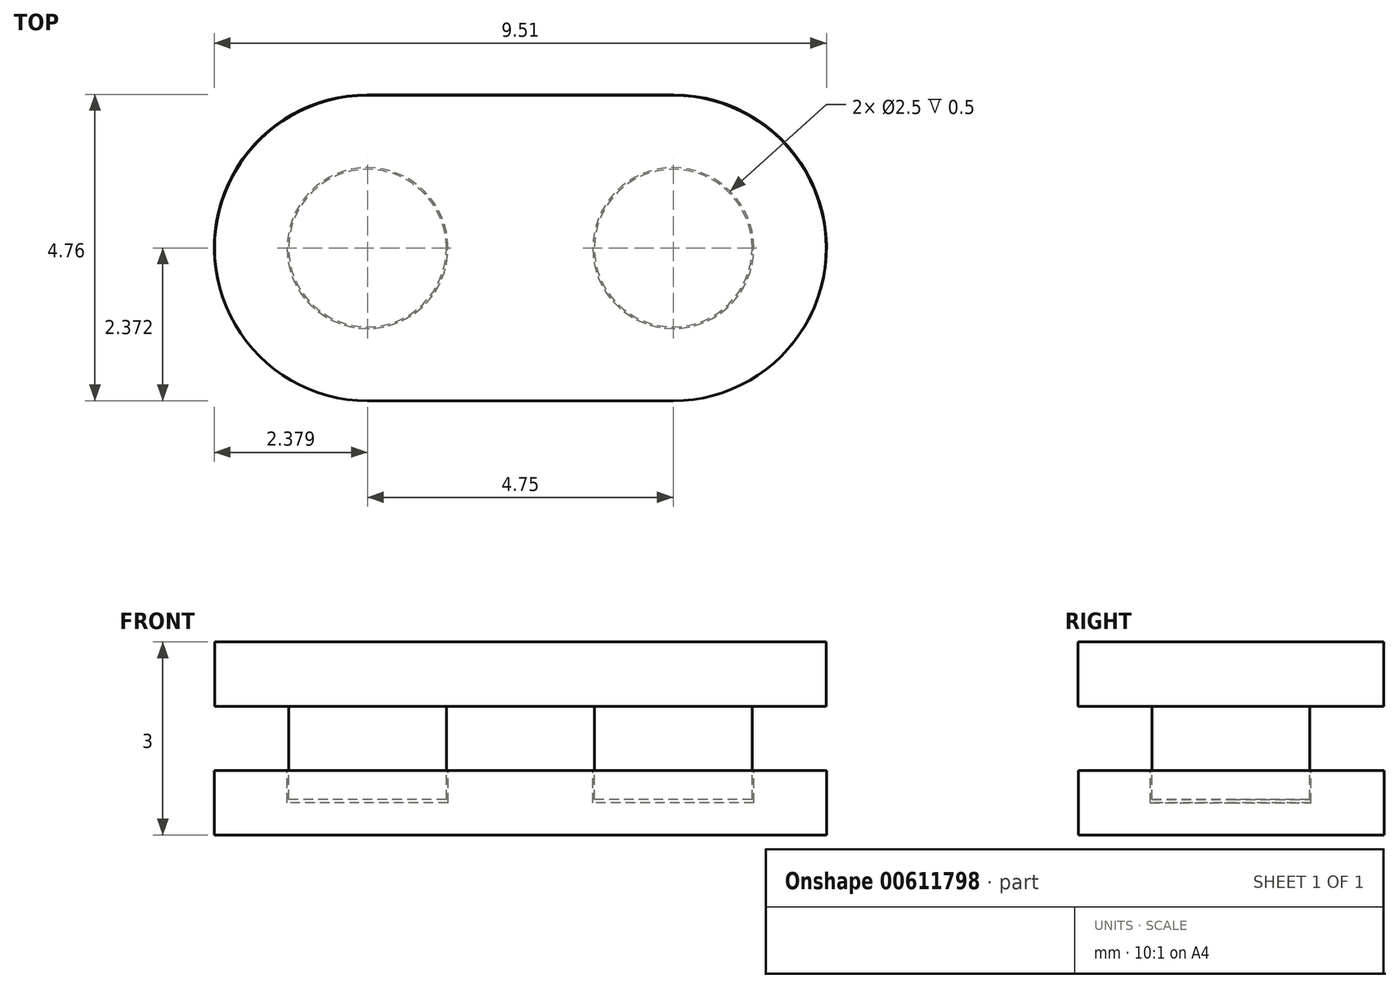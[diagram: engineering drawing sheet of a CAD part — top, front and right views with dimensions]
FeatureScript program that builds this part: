
annotation { "Feature Type Name" : "Feature", "Feature Type Description" : "" }
export const myFeature = defineFeature(function(context is Context, id is Id, definition is map)
    precondition{}
    {
        {
            var Q0;
            Q0=qCreatedBy(makeId("Top.planeOp"),FACE);
            var sketch = newSketch(context, id + "F0", { "sketchPlane" : qUnion([Q0])});
            skArc(sketch, "E0", {"start": v(2.64, -2.38) * mm, "mid": v(5.01, 0) * mm, "end": v(2.64, 2.37) * mm});
            skLineSegment(sketch, "E1", {"start": v(2.64, 2.37) * mm, "end": v(0.26, 2.37) * mm});
            skLineSegment(sketch, "E2", {"start": v(2.64, -2.38) * mm, "end": v(0.26, -2.38) * mm});
            skLineSegment(sketch, "E3.MirrorCS", {"start": v(-2.11, 2.37) * mm, "end": v(0.26, 2.37) * mm});
            skLineSegment(sketch, "E4.MirrorCS", {"start": v(-2.11, -2.38) * mm, "end": v(0.26, -2.38) * mm});
            skArc(sketch, "E5.MirrorC", {"start": v(-2.11, -2.38) * mm, "mid": v(-4.49, 0) * mm, "end": v(-2.11, 2.37) * mm});
            skCircle(sketch, "E6", {"center": v(-2.11, 0) * mm, "radius": 1.23 * mm});
            skCircle(sketch, "E7", {"center": v(2.64, 0) * mm, "radius": 1.23 * mm});
            skCircle(sketch, "E8", {"center": v(-2.11, 0) * mm, "radius": 1.25 * mm});
            skCircle(sketch, "E9", {"center": v(2.64, 0) * mm, "radius": 1.25 * mm});
            skSolve(sketch);
        }
        {
            var Q0;
            Q0 = qSketchRegion(id + "F0", true);
            var Q1;
            Q1=makeQuery(id+"F0.imprint","IMPRINT",FACE,{"disambiguationData":[TD([[makeQuery(id+"F0.imprint","IMPRINT",EDGE,{"derivedFrom":sQuery(id+"F0.wireOp",EDGE,"E6")}),1.0]])]});
            var Q2;
            Q2=makeQuery(id+"F0.imprint","IMPRINT",FACE,{"disambiguationData":[TD([[makeQuery(id+"F0.imprint","IMPRINT",EDGE,{"derivedFrom":sQuery(id+"F0.wireOp",EDGE,"E7")}),1.0]])]});
            var Q3;
            Q3=makeQuery(id+"F0.imprint","IMPRINT",FACE,{"disambiguationData":[TD([[makeQuery(id+"F0.imprint","IMPRINT",EDGE,{"derivedFrom":sQuery(id+"F0.wireOp",EDGE,"E7")}),-1.0]])]});
            var Q4;
            Q4=makeQuery(id+"F0.imprint","IMPRINT",FACE,{"disambiguationData":[TD([[makeQuery(id+"F0.imprint","IMPRINT",EDGE,{"derivedFrom":sQuery(id+"F0.wireOp",EDGE,"E6")}),-1.0]])]});
            extrude(context, id + "F1", {"entities" : qUnion([Q0, Q1, Q2, Q3, Q4]), "depth" : 1 * mm, "offsetDistance" : 25 * mm});
        }
        {
            var Q0;
            Q0=makeQuery(id+"F0.imprint","IMPRINT",FACE,{"disambiguationData":[TD([[makeQuery(id+"F0.imprint","IMPRINT",EDGE,{"derivedFrom":sQuery(id+"F0.wireOp",EDGE,"E7")}),1.0]])]});
            var Q1;
            Q1=makeQuery(id+"F0.imprint","IMPRINT",FACE,{"disambiguationData":[TD([[makeQuery(id+"F0.imprint","IMPRINT",EDGE,{"derivedFrom":sQuery(id+"F0.wireOp",EDGE,"E6")}),1.0]])]});
            extrude(context, id + "F2", {"entities" : qUnion([Q0, Q1]), "operationType" : NewBodyOperationType.ADD, "oppositeDirection" : true, "depth" : 1.5 * mm, "offsetDistance" : 25 * mm});
        }
        {
            var Q0;
            Q0=makeQuery(id+"F2.opExtrude","CAP_FACE",FACE,{"disambiguationData":[OSD([sQuery(id+"F0.wireOp",EDGE,"E6")])],"isStart":false});
            var sketch = newSketch(context, id + "F3", { "sketchPlane" : qUnion([Q0])});
            skArc(sketch, "E10", {"start": v(-2.12, 2.37) * mm, "mid": v(-4.5, 0) * mm, "end": v(-2.12, -2.38) * mm});
            skArc(sketch, "E11", {"start": v(2.65, -2.38) * mm, "mid": v(5.02, 0) * mm, "end": v(2.65, 2.38) * mm});
            skLineSegment(sketch, "E12", {"start": v(-2.12, 2.37) * mm, "end": v(2.65, 2.38) * mm});
            skLineSegment(sketch, "E13", {"start": v(-2.12, -2.38) * mm, "end": v(2.65, -2.37) * mm});
            skSolve(sketch);
        }
        {
            var Q0;
            Q0=makeQuery(id+"F3.imprint","IMPRINT",FACE,{"disambiguationData":[TD([[makeQuery(id+"F3.imprint","IMPRINT",EDGE,{"derivedFrom":sQuery(id+"F3.wireOp",EDGE,"E10")}),1.0]])]});
            var Q1;
            Q1=makeQuery(id+"F3.imprint","IMPRINT",FACE,{"disambiguationData":[TD([[makeQuery(id+"F3.imprint","IMPRINT",EDGE,{"derivedFrom":makeQuery(id+"F2.opExtrude","CAP_EDGE",EDGE,{"disambiguationData":[OSD([sQuery(id+"F0.wireOp",EDGE,"E6")])],"isStart":false})}),-1.0]])]});
            extrude(context, id + "F4", {"entities" : qUnion([Q0, Q1]), "depth" : .5 * mm, "offsetDistance" : 25 * mm, "hasSecondDirection" : true, "secondDirectionOppositeDirection" : true, "secondDirectionDepth" : .5 * mm});
        }
        {
            var Q0;
            Q0=makeQuery(id+"F0.imprint","IMPRINT",FACE,{"disambiguationData":[TD([[makeQuery(id+"F0.imprint","IMPRINT",EDGE,{"derivedFrom":sQuery(id+"F0.wireOp",EDGE,"E7")}),1.0]])]});
            var Q1;
            Q1=makeQuery(id+"F0.imprint","IMPRINT",FACE,{"disambiguationData":[TD([[makeQuery(id+"F0.imprint","IMPRINT",EDGE,{"derivedFrom":sQuery(id+"F0.wireOp",EDGE,"E6")}),1.0]])]});
            var Q2;
            Q2=makeQuery(id+"F0.imprint","IMPRINT",FACE,{"disambiguationData":[TD([[makeQuery(id+"F0.imprint","IMPRINT",EDGE,{"derivedFrom":sQuery(id+"F0.wireOp",EDGE,"E7")}),-1.0]])]});
            var Q3;
            Q3=makeQuery(id+"F0.imprint","IMPRINT",FACE,{"disambiguationData":[TD([[makeQuery(id+"F0.imprint","IMPRINT",EDGE,{"derivedFrom":sQuery(id+"F0.wireOp",EDGE,"E6")}),-1.0]])]});
            extrude(context, id + "F5", {"entities" : qUnion([Q0, Q1, Q2, Q3]), "operationType" : NewBodyOperationType.REMOVE, "oppositeDirection" : true, "depth" : 1.5 * mm, "offsetDistance" : 25 * mm});
        }
        {
            var Q0;
            Q0=makeQuery(id+"F0.imprint","IMPRINT",FACE,{"disambiguationData":[TD([[makeQuery(id+"F0.imprint","IMPRINT",EDGE,{"derivedFrom":sQuery(id+"F0.wireOp",EDGE,"E7")}),1.0]])]});
            var Q1;
            Q1=makeQuery(id+"F0.imprint","IMPRINT",FACE,{"disambiguationData":[TD([[makeQuery(id+"F0.imprint","IMPRINT",EDGE,{"derivedFrom":sQuery(id+"F0.wireOp",EDGE,"E6")}),1.0]])]});
            extrude(context, id + "F6", {"entities" : qUnion([Q0, Q1]), "operationType" : NewBodyOperationType.ADD, "oppositeDirection" : true, "depth" : 1.45 * mm, "offsetDistance" : 25 * mm});
        }
    });
